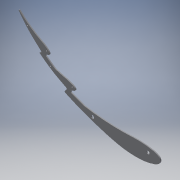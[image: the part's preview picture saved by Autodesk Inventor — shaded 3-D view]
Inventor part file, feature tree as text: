
AUTODESK INVENTOR PART (.ipt)
format: ipt  version: 2018.2 (Build 222227000, 227)  size: 199,168 bytes
history: native  units: mm
features: other x7, reference x6, projected_geometry x3, extrude x2, sketch x2, fillet x1
ambient origin geometry x8: Origin, YZ Plane, XZ Plane, XY Plane, X Axis, Y Axis, Z Axis, Center Point
bodies: Body1 (feature_tree)
feature tree (21):
  extrude  "押し出し1"  TaperAngle=45.0deg  [1 undecoded]
  fillet  "フィレット1"  [1 undecoded]
  extrude  "押し出し2"  Depth=60.0mm
  sketch  "スケッチ1"
  projected_geometry  "投影ループ1"
  projected_geometry  "投影ループ2"
  projected_geometry  "投影ループ3"
  sketch  "スケッチ2"
  reference  "参照1"
  reference  "参照2"
  reference  "参照3"
  reference  "参照4"
  reference  "参照5"
  reference  "参照6"
  other  "<userpath>\Documents\Inventor\Aero\KS-15\Rr.wing\Rr.wing_assy.iam"
  other  "Rr.wing_assy.iam"
  other  "mainflap:1"
  other  "flap_m:1"
  other  "subflap:3"
  other  "flap_s:1"
  other  "subflap:8"
note: 2 required parameter values undecoded (feature->parameter linkage not recoverable at this tier; creation-order binding heuristic only, values carry confidence <= 0.55)
